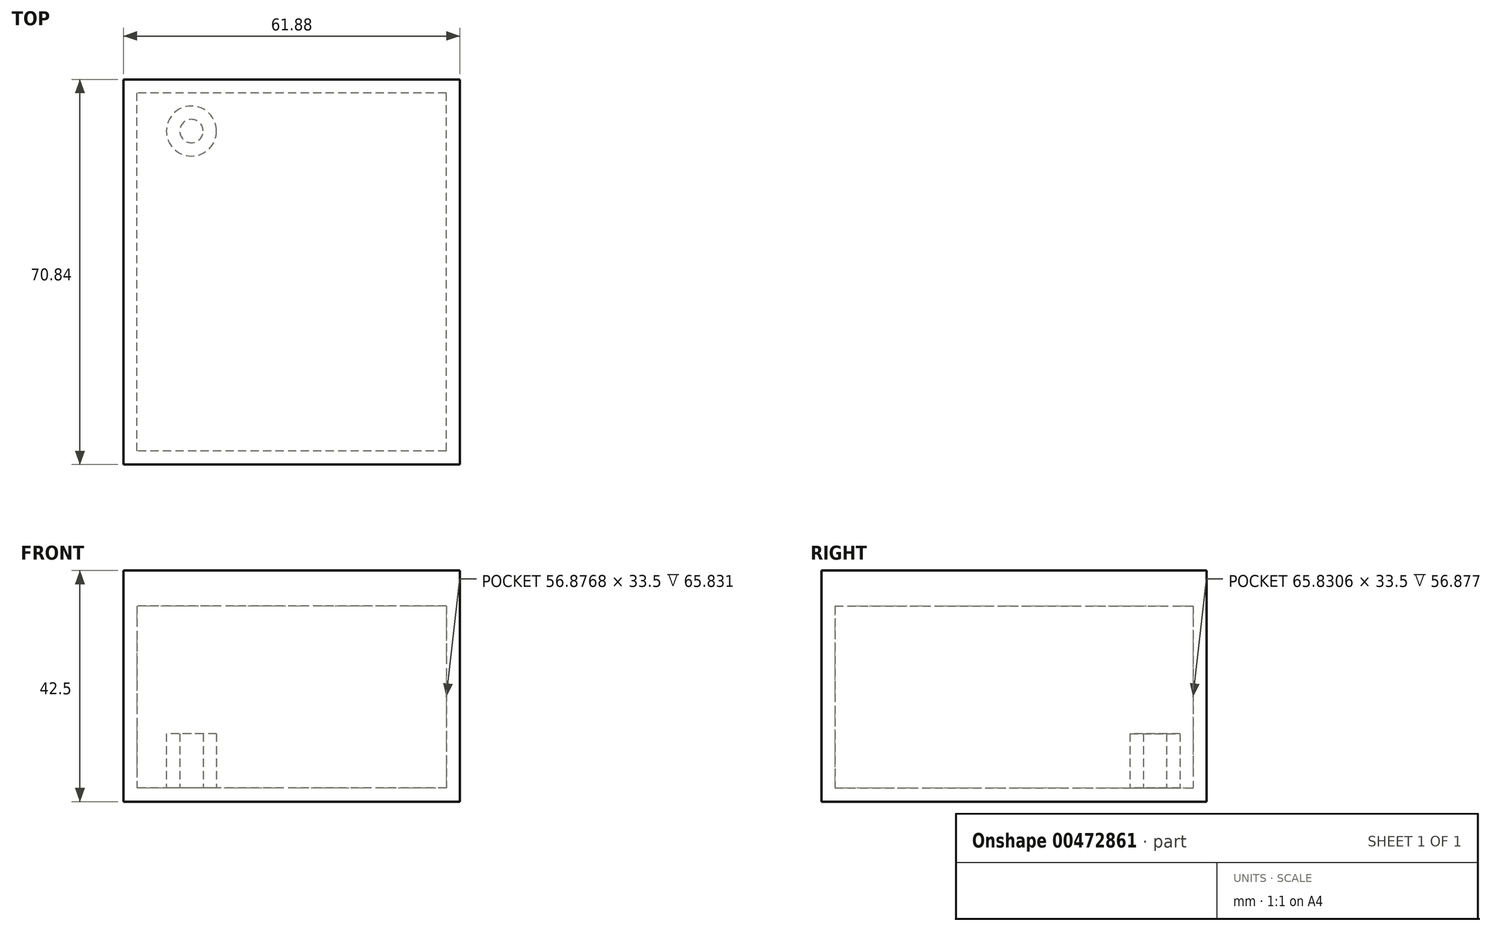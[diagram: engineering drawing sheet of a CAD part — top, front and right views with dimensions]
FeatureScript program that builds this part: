
annotation { "Feature Type Name" : "Feature", "Feature Type Description" : "" }
export const myFeature = defineFeature(function(context is Context, id is Id, definition is map)
    precondition{}
    {
        {
            assignVariable(context, id + "F0", {"name" : "hautboit", "anyValue" : 40});
        }
        {
            var Q0;
            Q0=qCreatedBy(makeId("Top.planeOp"),FACE);
            var sketch = newSketch(context, id + "F1", { "sketchPlane" : qUnion([Q0])});
            skLineSegment(sketch, "E0.bottom", {"start": v(30.94, -35.42) * mm, "end": v(-30.94, -35.42) * mm});
            skLineSegment(sketch, "E0.top", {"start": v(30.94, 35.42) * mm, "end": v(-30.94, 35.42) * mm});
            skLineSegment(sketch, "E0.left", {"start": v(30.94, -35.42) * mm, "end": v(30.94, 35.42) * mm});
            skLineSegment(sketch, "E0.right", {"start": v(-30.94, -35.42) * mm, "end": v(-30.94, 35.42) * mm});
            skPoint(sketch, "E0.middle", {"position": v(0, 0) * mm});
            skSolve(sketch);
        }
        {
            var Q0;
            Q0=makeQuery(id+"F1.imprint","IMPRINT",FACE,{"disambiguationData":[TD([[makeQuery(id+"F1.imprint","IMPRINT",EDGE,{"derivedFrom":sQuery(id+"F1.wireOp",EDGE,"E0.bottom")}),-1.0]])]});
            extrude(context, id + "F2", {"entities" : qUnion([Q0]), "depth" : (getVariable(context, 'hautboit')) * mm});
        }
        {
            var Q0;
            Q0=makeQuery(id+"F2.opExtrude","CAP_FACE",FACE,{"disambiguationData":[OSD([sQuery(id+"F1.wireOp",EDGE,"E0.bottom"),sQuery(id+"F1.wireOp",EDGE,"E0.top"),sQuery(id+"F1.wireOp",EDGE,"E0.left"),sQuery(id+"F1.wireOp",EDGE,"E0.right")])],"isStart":false});
            shell(context, id + "F3", {"entities" : qUnion([Q0]), "thickness" : 2.5 * mm});
        }
        {
            var Q0;
            Q0=makeQuery(id+"F2.opExtrude","CAP_FACE",FACE,{"disambiguationData":[OSD([sQuery(id+"F1.wireOp",EDGE,"E0.bottom"),sQuery(id+"F1.wireOp",EDGE,"E0.top"),sQuery(id+"F1.wireOp",EDGE,"E0.left"),sQuery(id+"F1.wireOp",EDGE,"E0.right")])],"isStart":false});
            var sketch = newSketch(context, id + "F4", { "sketchPlane" : qUnion([Q0])});
            skLineSegment(sketch, "E1.bottom", {"start": v(-28.44, 32.92) * mm, "end": v(28.44, 32.92) * mm});
            skLineSegment(sketch, "E1.top", {"start": v(-28.44, -32.92) * mm, "end": v(28.44, -32.92) * mm});
            skLineSegment(sketch, "E1.left", {"start": v(-28.44, 32.92) * mm, "end": v(-28.44, -32.92) * mm});
            skLineSegment(sketch, "E1.right", {"start": v(28.44, 32.92) * mm, "end": v(28.44, -32.92) * mm});
            skLineSegment(sketch, "E2.bottom", {"start": v(-30.94, 35.42) * mm, "end": v(30.94, 35.42) * mm});
            skLineSegment(sketch, "E2.top", {"start": v(-30.94, -35.42) * mm, "end": v(30.94, -35.42) * mm});
            skLineSegment(sketch, "E2.left", {"start": v(-30.94, 35.42) * mm, "end": v(-30.94, -35.42) * mm});
            skLineSegment(sketch, "E2.right", {"start": v(30.94, 35.42) * mm, "end": v(30.94, -35.42) * mm});
            skSolve(sketch);
        }
        {
            var Q0;
            Q0=makeQuery(id+"F4.imprint","IMPRINT",FACE,{"disambiguationData":[TD([[makeQuery(id+"F4.imprint","IMPRINT",EDGE,{"derivedFrom":sQuery(id+"F4.wireOp",EDGE,"E1.bottom")}),-1.0]])]});
            var Q1;
            Q1=makeQuery(id+"F4.imprint","IMPRINT",FACE,{"disambiguationData":[TD([[makeQuery(id+"F4.imprint","IMPRINT",EDGE,{"derivedFrom":sQuery(id+"F4.wireOp",EDGE,"E1.bottom")}),1.0]])]});
            extrude(context, id + "F5", {"entities" : qUnion([Q0, Q1]), "depth" : 2.5 * mm});
        }
        {
            var Q0;
            Q0=makeQuery(id+"F4.imprint","IMPRINT",FACE,{"disambiguationData":[TD([[makeQuery(id+"F4.imprint","IMPRINT",EDGE,{"derivedFrom":sQuery(id+"F4.wireOp",EDGE,"E1.bottom")}),1.0]])]});
            extrude(context, id + "F6", {"entities" : qUnion([Q0]), "operationType" : NewBodyOperationType.ADD, "oppositeDirection" : true, "depth" : 4 * mm});
        }
        {
            var Q0;
            Q0=makeQuery(id+"F3.opShell","OFFSET_FACE",FACE,{"disambiguationData":[OSD([sQuery(id+"F1.wireOp",EDGE,"E0.bottom"),sQuery(id+"F1.wireOp",EDGE,"E0.top"),sQuery(id+"F1.wireOp",EDGE,"E0.left"),sQuery(id+"F1.wireOp",EDGE,"E0.right")])]});
            var sketch = newSketch(context, id + "F7", { "sketchPlane" : qUnion([Q0])});
            skCircle(sketch, "E3", {"center": v(-18.44, 25.92) * mm, "radius": 2.15 * mm});
            skCircle(sketch, "E4", {"center": v(-18.44, 25.92) * mm, "radius": 4.6 * mm});
            skSolve(sketch);
        }
        {
            var Q0;
            Q0=makeQuery(id+"F7.imprint","IMPRINT",FACE,{"disambiguationData":[TD([[makeQuery(id+"F7.imprint","IMPRINT",EDGE,{"derivedFrom":sQuery(id+"F7.wireOp",EDGE,"E3")}),-1.0]])]});
            extrude(context, id + "F8", {"entities" : qUnion([Q0]), "operationType" : NewBodyOperationType.ADD, "depth" : 10 * mm});
        }
    });
